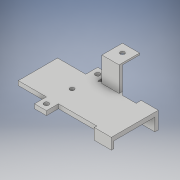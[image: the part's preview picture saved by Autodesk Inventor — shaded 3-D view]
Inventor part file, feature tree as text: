
AUTODESK INVENTOR PART (.ipt)
format: ipt  version: 2018 (Build 220112000, 112)  size: 270,848 bytes
history: native  units: in
note: dims shown in document units (in); Inventor stores cm internally (conversion verified against a paired STEP export)
features: extrude x15, sketch x15, projected_geometry x2, chamfer x1
ambient origin geometry x8: Origin, YZ Plane, XZ Plane, XY Plane, X Axis, Y Axis, Z Axis, Center Point
bodies: Solid1 (feature_tree)
feature tree (33):
  extrude  "Extrusion1"  Depth=0.3937in
  extrude  "Extrusion2"  Depth=0.0394in TaperAngle=0.0deg
  extrude  "Extrusion3"  Depth=0.0394in TaperAngle=0.0deg
  extrude  "Extrusion4"  Depth=0.6693in TaperAngle=0.0deg
  extrude  "Extrusion5"  TaperAngle=0.0deg  [1 undecoded]
  extrude  "Extrusion10"  Depth=2.2047in
  extrude  "Extrusion11"  TaperAngle=0.0deg  [1 undecoded]
  extrude  "Extrusion12"  Depth=0.7874in
  extrude  "Extrusion13"  Depth=0.7874in
  extrude  "Extrusion14"  TaperAngle=0.0deg  [1 undecoded]
  extrude  "Extrusion18"  Depth=0.2756in
  extrude  "Extrusion23"  Depth=0.2756in
  extrude  "Extrusion24"  Depth=0.1083in
  extrude  "Extrusion25"  TaperAngle=0.0deg  [1 undecoded]
  extrude  "Extrusion26"  Depth=0.3937in
  chamfer  "Chamfer1"  Distance=0.3937in
  sketch  "Sketch1"  dims[d0=0.3937in d1=0.3937in]
  sketch  "Sketch2"  dims[d2=0.1181in d3=0.0394in d4=0.0in]
  sketch  "Sketch3"  dims[d5=0.0591in d6=0.0394in d7=0.0in]
  sketch  "Sketch4"  dims[d8=0.0591in d9=0.6693in d10=0.0in]
  sketch  "Sketch5"  dims[d11=0.0591in d12=0.0in d13=0.0in]
  sketch  "Sketch11"  dims[d14=0.0591in d15=2.2047in]
  sketch  "Sketch12"  dims[d16=0.9055in d17=0.0in d42=0.0in]
  sketch  "Sketch13"  dims[d45=0.0984in d46=0.7874in]
  sketch  "Sketch14"  dims[d47=0.0394in d48=0.0in d49=0.7874in]
  sketch  "Sketch15"  dims[d50=0.0in d51=0.0in]
  sketch  "Sketch19"  dims[d52=0.2756in d53=0.2756in]
  sketch  "Sketch24"  dims[d54=0.2756in d55=0.2756in]
  sketch  "Sketch25"  dims[d56=0.1083in d57=0.1083in]
  projected_geometry  "Projected Loop2"
  sketch  "Sketch26"  dims[d58=0.0984in d59=0.0in d60=0.0in]
  sketch  "Sketch27"  dims[d61=0.1181in d62=0.3937in d63=0.3937in d64=0.0in d65=0.0394in d66=0.0in d67=0.1575in d68=0.0in d69=0.7874in d70=0.0in d80=1.1811in d81=0.0in d95=0.7874in d96=0.3937in d97=0.0787in d98=0.5709in d99=0.0in d100=0.0984in d101=0.0in d102=0.0394in d103=0.3937in d104=0.0in d105=0.0984in d106=0.3937in d107=0.0in d108=0.0787in d109=0.125in d110=45.0deg]
  projected_geometry  "Projected Loop3"
note: 4 required parameter values undecoded (feature->parameter linkage not recoverable at this tier; creation-order binding heuristic only, values carry confidence <= 0.55)
